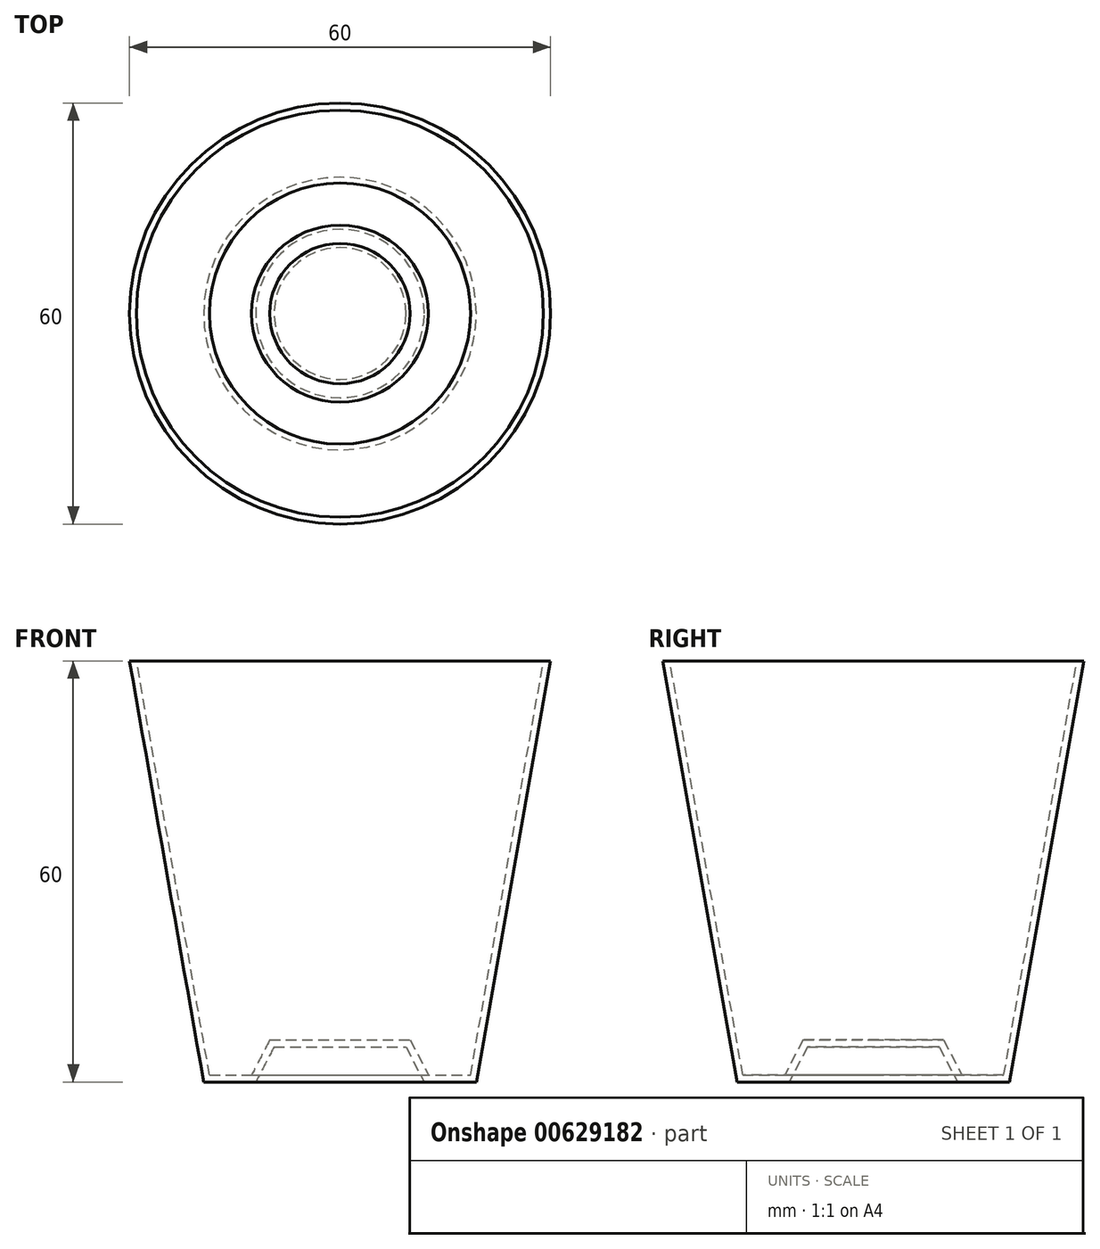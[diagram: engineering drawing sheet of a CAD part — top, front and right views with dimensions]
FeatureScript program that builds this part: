
annotation { "Feature Type Name" : "Feature", "Feature Type Description" : "" }
export const myFeature = defineFeature(function(context is Context, id is Id, definition is map)
    precondition{}
    {
        {
            var Q0;
            Q0=qCreatedBy(makeId("Front.planeOp"),FACE);
            var sketch = newSketch(context, id + "F0", { "sketchPlane" : qUnion([Q0])});
            skLineSegment(sketch, "E0", {"start": v(12, 0) * mm, "end": v(19.42, 0) * mm});
            skLineSegment(sketch, "E1", {"start": v(19.42, 0) * mm, "end": v(30, 60) * mm});
            skLineSegment(sketch, "E2", {"start": v(30, 60) * mm, "end": v(29, 60) * mm});
            skLineSegment(sketch, "E3", {"start": v(29, 60) * mm, "end": v(18.6, 1) * mm});
            skLineSegment(sketch, "E4", {"start": v(18.6, 1) * mm, "end": v(12.6, 1) * mm});
            skLineSegment(sketch, "E5", {"start": v(9.4, 5) * mm, "end": v(12, 0) * mm});
            skLineSegment(sketch, "E6", {"start": v(12.6, 1) * mm, "end": v(10, 6) * mm});
            skLineSegment(sketch, "E7", {"start": v(10, 6) * mm, "end": v(0, 6) * mm});
            skLineSegment(sketch, "E8", {"start": v(9.4, 5) * mm, "end": v(0, 5) * mm});
            skLineSegment(sketch, "E9", {"start": v(0, 5) * mm, "end": v(0, 6) * mm});
            skSolve(sketch);
        }
        {
            var Q0;
            Q0 = qSketchRegion(id + "F0", true);
            var Q1;
            Q1=sQuery(id+"F0.wireOp",EDGE,"E9");
            revolve(context, id + "F1", {"entities" : qUnion([Q0]), "axis" : qUnion([Q1]), "revolveType" : RevolveType.FULL});
        }
    });
